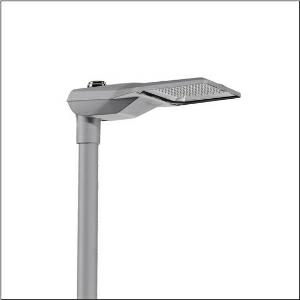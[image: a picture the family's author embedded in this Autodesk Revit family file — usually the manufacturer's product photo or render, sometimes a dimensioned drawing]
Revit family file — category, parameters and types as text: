
# Revit family: streetlight_sl_21_midi___st1_0a_5xe7d47n08nb_e9e4
name_source: partatom
category: Lighting Fixtures
units: mm (PartAtom-declared; Revit-internal decimal feet)

## family parameters
Cut with Voids When Loaded = No
Host = Face
Light Source = No
Part Type = Normal
Room Calculation Point = No
Round Connector Dimension = Use Diameter
Shared = No

## types (1)
- --- (1 x LED, 23710 lm, 151.2 W, 4000K)
    Apparent Load = 151 VA
    CIE Flux Codes = 40 73 97 100 100
    Color Rendering = 70
    Color Temperature = 4000K
    Default Elevation = 1800 mm
    Description = Streetlight SL 21 midi, mast luminaire, primary light control with lens, of PMMA, primary optical cover: cover, of toughened safety glass, transparent, light distribution: ST1.0a, light emission: direct distribution, primary light characteristic: asymmetric, installation type: side-entry, LED, 3G 2.5mm², High Power LED, rated luminous flux: 23.710lm, luminous efficacy: 157lm/W, light colour: 740, colour temperature: 4000K, control gear: NEMA (7pin), control: overheat protection, pre-setting: linear dimming characteristic, constant luminous flux control, time-dependent luminous flux control, flexible luminous flux parameterisation, mains connection: 220..240V, AC, 50/60Hz, connection cable pre-assembled, cable length: 12,5m, wiring characteristics: H05VV-F, start of lifetime: 151W, end of service life: 157W, reduction: 70W, luminaire housing, of diecast aluminium (EN AC-44300), powder-coated, Siteco® metallic grey (DB 702S), corrosivity category C5 mid according to DIN EN ISO 12944, multi-level sealing system, sealing non-destructively replaceable, inclination adjustable: 0°, 5°, 10°, 15°, length: 644mm, width: 335mm, height: 110mm, spigot size: 42mm (side-entry), mounting height: 4..8m, protection rating (complete): IP66, insulation class (complete): insulation class I (protective earthing), certification: CE, ENEC, ENEC+, VDE, impact resistance: IK10, permissible operating ambient temperature for outdoor applications: -40..+50°C, standard-compliant lighting for roads and squares, packaging unit: 1 piece

Light Distribution: ST1.0a
    Height = 111 mm
    Lamp = 1 x LED
    Lamp Light Flux = 23710 lm
    Lamp Power = 151.2 W
    Lamp count = 1
    Length = 644 mm
    Luminous efficacy = 157 lm/W
    Manufacturer = Siteco
    ModVariant = No
    Model = 5XE7D47N08NB
    Number of Poles = 1
    OnlyDefault = Yes
    Power Factor = 1
    Product Name = Streetlight SL 21 midi | ST1.0a
    Product group = mast luminaire | pylon top
    ProductGroupID = 6100
    Protection Class = Protection class I
    Protection Degree = IP 66
    RLX_Detail_Level = 1
    RLX_Emergency_Light_Flux = 0 lm
    RLX_Emergency_Type = 0
    RLX_Emergency_Type_DB = No
    RlxData = <blob elided: 26673 chars, md5=b8a74c9a>
    Socket = socket
    Standby Power = 0 W
    System Light Flux = 23710 lm
    System Power = 151 W
    Type Comments = factory setting: luminous flux: 100 % | dim-lin: 254 | 802 mA
    Type Image = l_1294377.jpg
    URL = http://relux.com
    VarID = @adj_156607
    Voltage = 0 V
    Weight = 0.00 kg
    Width = 336 mm

## geometry (parser evidence)
native form markers: Blend x4, Sweep x10
no freeform markers — native parametric forms only
